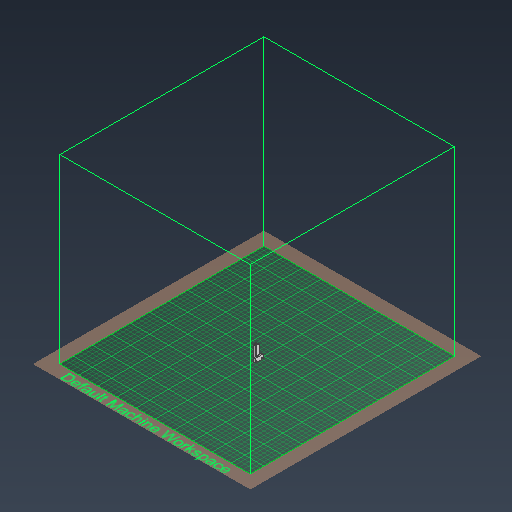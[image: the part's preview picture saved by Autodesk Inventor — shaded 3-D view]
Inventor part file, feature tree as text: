
AUTODESK INVENTOR PART (.ipt)
format: ipt  version: 2021 (Build 250183000, 183)  size: 338,944 bytes
history: native  units: mm
features: sketch x5, extrude x4, fillet x1
ambient origin geometry x8: Origin, YZ Plane, XZ Plane, XY Plane, X Axis, Y Axis, Z Axis, Center Point
bodies: Solid1 (feature_tree)
feature tree (10):
  extrude  "Extrusion1"  Depth=8.0mm
  sketch  "Sketch2"  dims[d2=35.0mm d3=0.0mm d4=4.95mm]
  extrude  "Extrusion2"  Depth=4.95mm
  extrude  "Extrusion3"  Depth=3.0mm
  extrude  "Extrusion4"  Depth=10.0mm
  fillet  "Fillet2"  Radius=10.0mm
  sketch  "Sketch1"  dims[d0=6.0mm d1=8.0mm]
  sketch  "Sketch3"  dims[d5=2.95mm d6=3.0mm]
  sketch  "Sketch4"  dims[d7=2.475mm d9=1.475mm d10=10.0mm d11=0.0mm]
  sketch  "Sketch5"  dims[d12=4.0mm d13=9.525mm d14=17.78mm d15=4.89mm d16=3.175mm d17=0.0mm d18=2.1844mm d19=2.1844mm d20=12.7mm d21=2.54mm d22=3.75mm d23=0.0mm d26=3.175mm d27=3.175mm d28=1.0mm]
